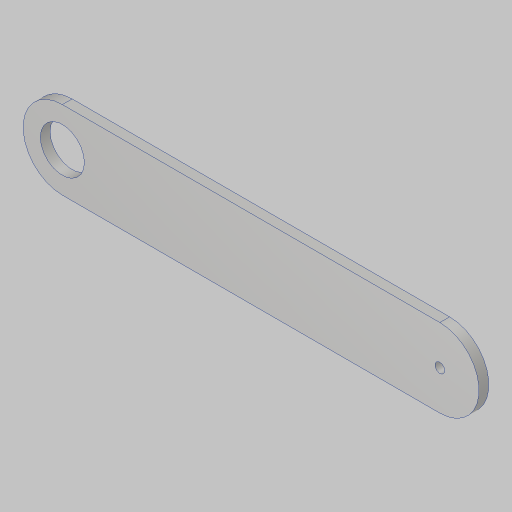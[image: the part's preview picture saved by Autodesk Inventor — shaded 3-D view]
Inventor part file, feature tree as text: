
AUTODESK INVENTOR PART (.ipt)
format: ipt  version: 2023.5 (Build 275446000, 446)  size: 101,888 bytes
history: native  units: in
note: dims shown in document units (in); Inventor stores cm internally (conversion verified against a paired STEP export)
features: extrude x1, sketch x1
ambient origin geometry x8: Origin, YZ Plane, XZ Plane, XY Plane, X Axis, Y Axis, Z Axis, Center Point
bodies: Solid1 (feature_tree)
feature tree (2):
  extrude  "Extrusion1"  Depth=9.625in
  sketch  "Sketch1"  dims[d0=1.125in d1=9.625in d2=2.0in d3=0.25in d4=0.25in d5=0.0in]
